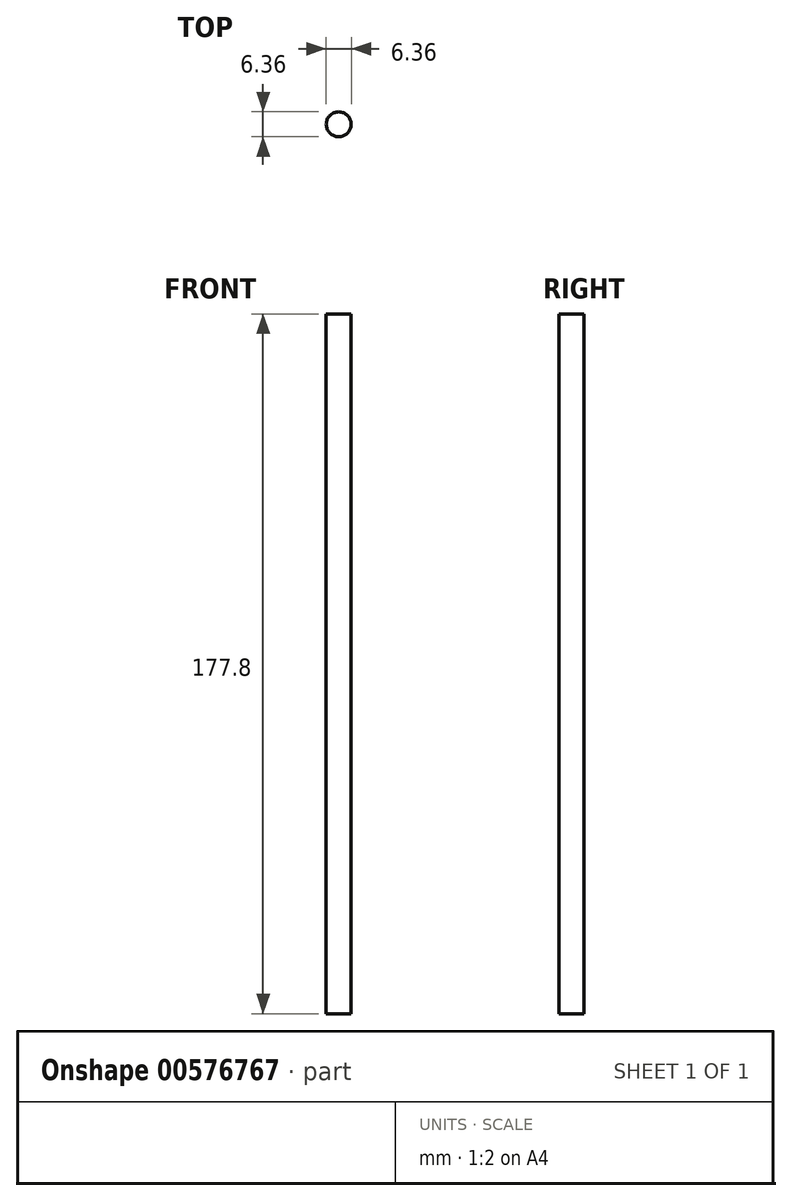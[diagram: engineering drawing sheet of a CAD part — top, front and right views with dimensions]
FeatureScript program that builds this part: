
annotation { "Feature Type Name" : "Feature", "Feature Type Description" : "" }
export const myFeature = defineFeature(function(context is Context, id is Id, definition is map)
    precondition{}
    {
        {
            var Q0;
            Q0=qCreatedBy(makeId("Top.planeOp"),FACE);
            var sketch = newSketch(context, id + "F0", { "sketchPlane" : qUnion([Q0])});
            skCircle(sketch, "E0", {"center": v(0, 0) * mm, "radius": 3.18 * mm});
            skSolve(sketch);
        }
        {
            var Q0;
            Q0 = qSketchRegion(id + "F0", true);
            extrude(context, id + "F1", {"entities" : qUnion([Q0]), "depth" : 177.8 * mm, "offsetDistance" : 25.4 * mm});
        }
    });
